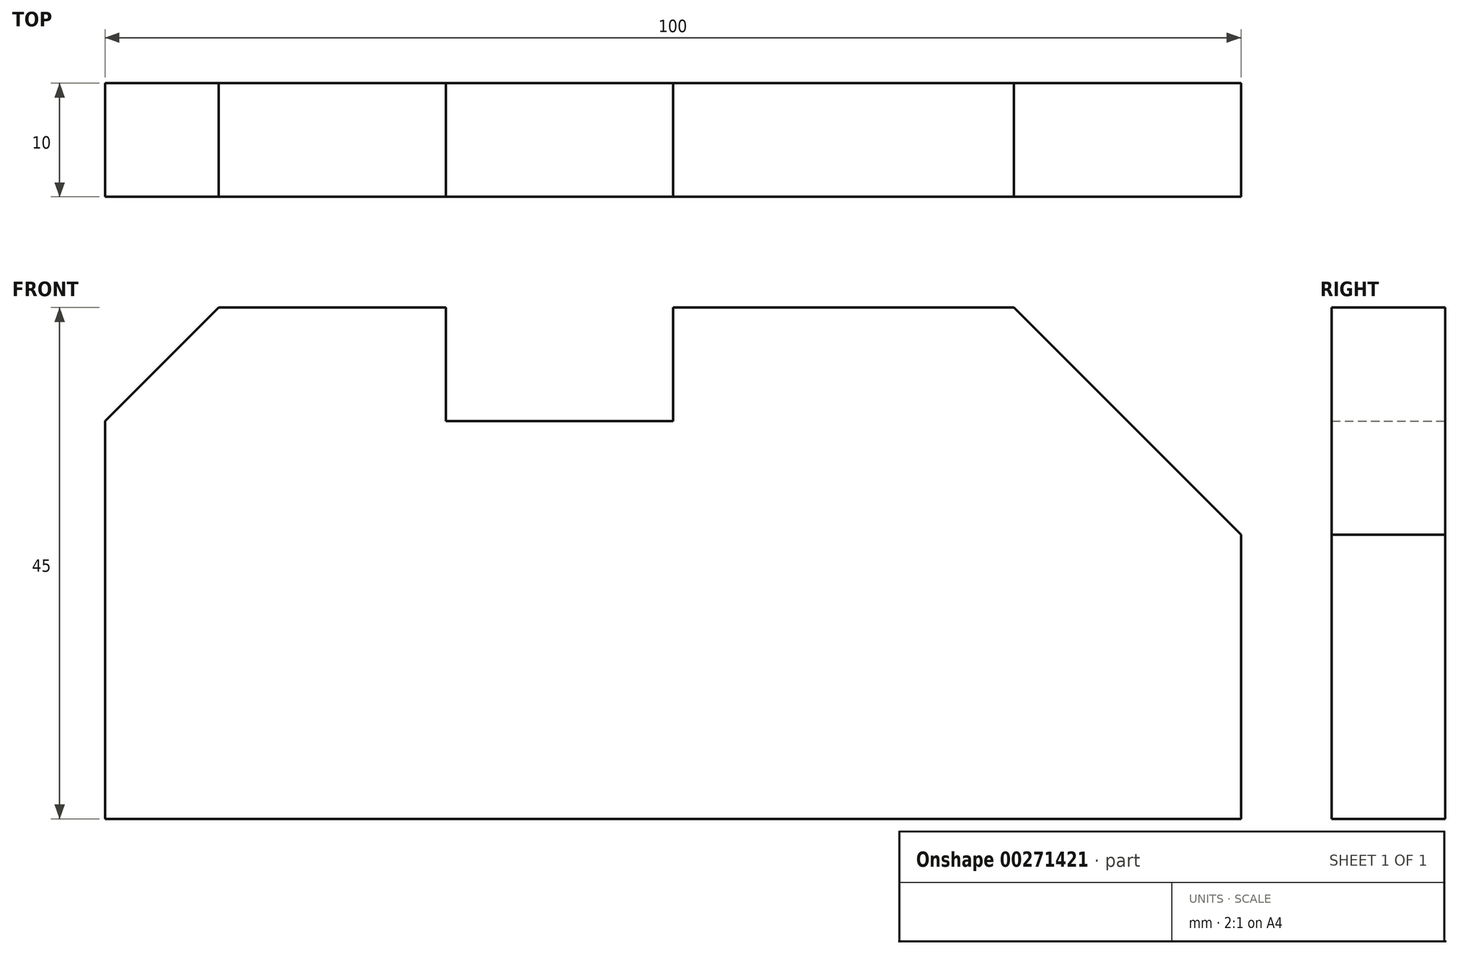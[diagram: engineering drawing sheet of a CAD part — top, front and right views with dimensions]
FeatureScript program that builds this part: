
annotation { "Feature Type Name" : "Feature", "Feature Type Description" : "" }
export const myFeature = defineFeature(function(context is Context, id is Id, definition is map)
    precondition{}
    {
        {
            var Q0;
            Q0=qCreatedBy(makeId("Front.planeOp"),FACE);
            var sketch = newSketch(context, id + "F0", { "sketchPlane" : qUnion([Q0])});
            skLineSegment(sketch, "E0", {"start": v(0, 0) * mm, "end": v(0, 35) * mm});
            skLineSegment(sketch, "E1", {"start": v(0, 35) * mm, "end": v(10, 45) * mm});
            skLineSegment(sketch, "E2", {"start": v(10, 45) * mm, "end": v(30, 45) * mm});
            skLineSegment(sketch, "E3", {"start": v(30, 45) * mm, "end": v(30, 35) * mm});
            skLineSegment(sketch, "E4", {"start": v(30, 35) * mm, "end": v(50, 35) * mm});
            skLineSegment(sketch, "E5", {"start": v(50, 35) * mm, "end": v(50, 45) * mm});
            skLineSegment(sketch, "E6", {"start": v(50, 45) * mm, "end": v(80, 45) * mm});
            skLineSegment(sketch, "E7", {"start": v(80, 45) * mm, "end": v(100, 25) * mm});
            skLineSegment(sketch, "E8", {"start": v(100, 25) * mm, "end": v(100, 0) * mm});
            skLineSegment(sketch, "E9", {"start": v(0, 0) * mm, "end": v(100, 0) * mm});
            skSolve(sketch);
        }
        {
            var Q0;
            Q0 = qSketchRegion(id + "F0", true);
            extrude(context, id + "F1", {"entities" : qUnion([Q0]), "depth" : 10 * mm});
        }
    });
